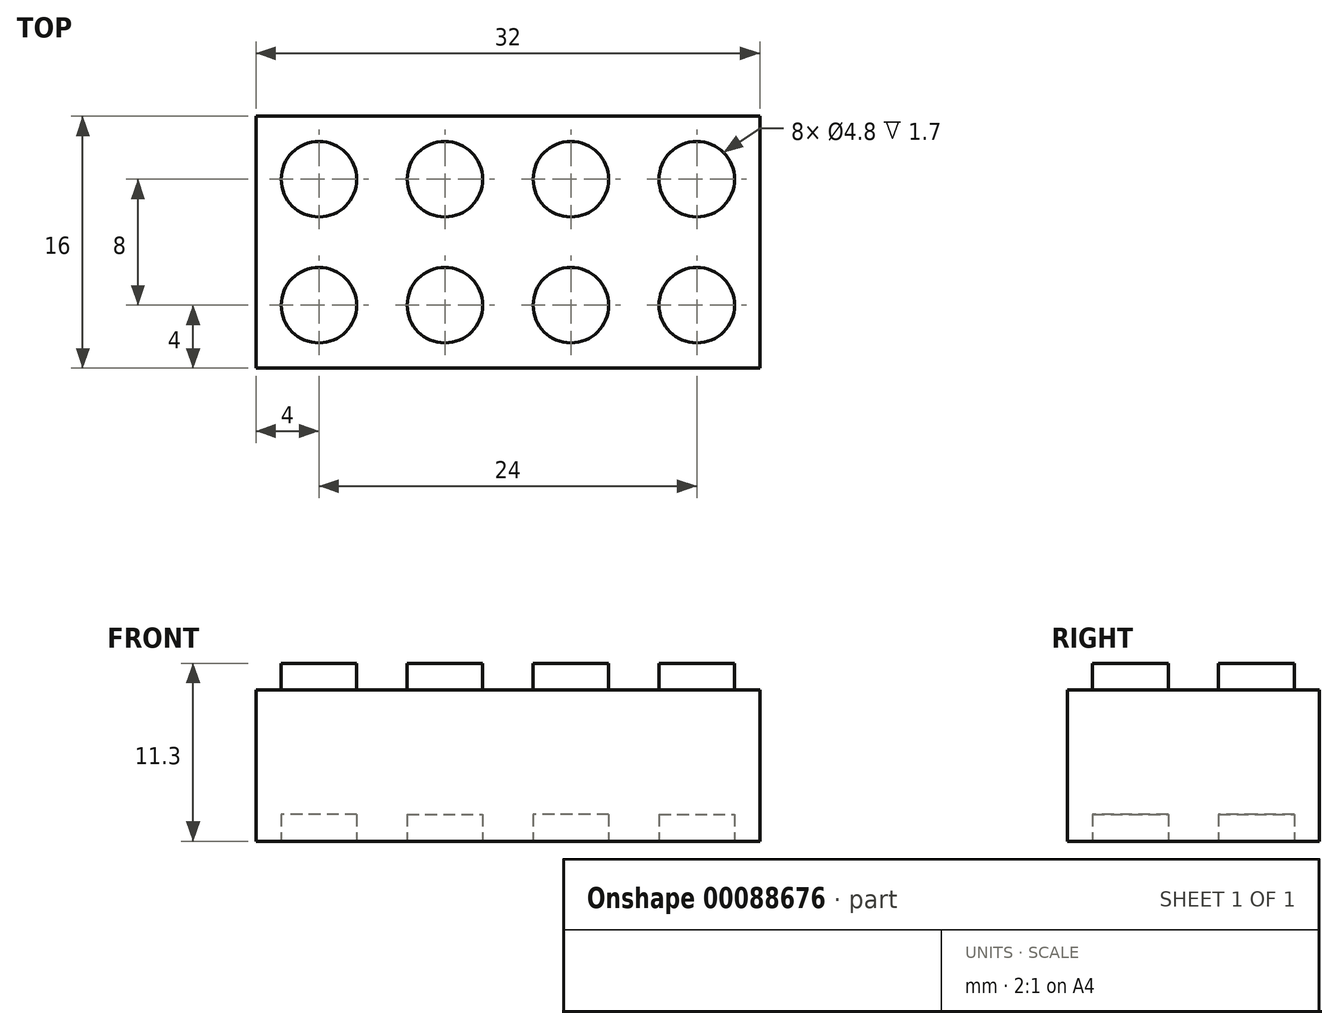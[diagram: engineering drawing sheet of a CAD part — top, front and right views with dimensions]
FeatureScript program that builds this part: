
annotation { "Feature Type Name" : "Feature", "Feature Type Description" : "" }
export const myFeature = defineFeature(function(context is Context, id is Id, definition is map)
    precondition{}
    {
        {
            var Q0;
            Q0=qCreatedBy(makeId("Front.planeOp"),FACE);
            var sketch = newSketch(context, id + "F0", { "sketchPlane" : qUnion([Q0])});
            skLineSegment(sketch, "E0.bottom", {"start": v(-4, 9.6) * mm, "end": v(-2.4, 9.6) * mm});
            skLineSegment(sketch, "E0.top", {"start": v(-4, 0) * mm, "end": v(4, 0) * mm});
            skLineSegment(sketch, "E0.left", {"start": v(-4, 9.6) * mm, "end": v(-4, 0) * mm});
            skLineSegment(sketch, "E0.right", {"start": v(4, 9.6) * mm, "end": v(4, 0) * mm});
            skLineSegment(sketch, "E1.top", {"start": v(-2.4, 11.3) * mm, "end": v(2.4, 11.3) * mm});
            skLineSegment(sketch, "E1.left", {"start": v(-2.4, 9.6) * mm, "end": v(-2.4, 11.3) * mm});
            skLineSegment(sketch, "E1.right", {"start": v(2.4, 9.6) * mm, "end": v(2.4, 11.3) * mm});
            skLineSegment(sketch, "E2", {"start": v(0, 0) * mm, "end": v(0, 24.04) * mm, "construction": true});
            skLineSegment(sketch, "E3.trimOffspring", {"start": v(2.4, 9.6) * mm, "end": v(4, 9.6) * mm});
            skSolve(sketch);
        }
        {
            var Q0;
            Q0=makeQuery(id+"F0.imprint","IMPRINT",FACE,{"disambiguationData":[TD([[makeQuery(id+"F0.imprint","IMPRINT",EDGE,{"derivedFrom":sQuery(id+"F0.wireOp",EDGE,"E0.bottom")}),-1.0]])]});
            extrude(context, id + "F1", {"entities" : qUnion([Q0]), "depth" : 8 * mm});
        }
        {
            var Q0;
            Q0=qCreatedBy(makeId("Top.planeOp"),FACE);
            var Q1;
            Q1=makeQuery(id+"F1.opExtrude","CAP_VERTEX",VERTEX,{"disambiguationData":[OSD([sQuery(id+"F0.wireOp",EDGE,"E1.top"),sQuery(id+"F0.wireOp",EDGE,"E1.right")])],"isStart":true});
            cPlane(context, id + "F2", {"entities" : qUnion([Q0, Q1]), "cplaneType" : CPlaneType.PLANE_POINT, "offset" : 152.4 * mm, "width" : 152.4 * mm, "height" : 152.4 * mm});
        }
        {
            var Q0;
            Q0=qCreatedBy(id+"F2.planeOp",FACE);
            var sketch = newSketch(context, id + "F3", { "sketchPlane" : qUnion([Q0])});
            skLineSegment(sketch, "E4.0", {"start": v(-4, -8) * mm, "end": v(-4, 0) * mm});
            skLineSegment(sketch, "E5.0", {"start": v(4, -8) * mm, "end": v(4, 0) * mm});
            skLineSegment(sketch, "E6", {"start": v(-4, 0) * mm, "end": v(4, 0) * mm});
            skLineSegment(sketch, "E7", {"start": v(-4, -8) * mm, "end": v(4, -8) * mm});
            skLineSegment(sketch, "E8", {"start": v(-4, 0) * mm, "end": v(4, -8) * mm, "construction": true});
            skLineSegment(sketch, "E9", {"start": v(-4, -8) * mm, "end": v(4, 0) * mm, "construction": true});
            skCircle(sketch, "E10", {"center": v(0, -4) * mm, "radius": 2.4 * mm});
            skSolve(sketch);
        }
        {
            var Q0;
            Q0=qSketchRegion(id+"F3",true);
            var Q1;
            Q1=makeQuery(id+"F1.opExtrude","SWEPT_FACE",FACE,{"disambiguationData":[OSD([sQuery(id+"F0.wireOp",EDGE,"E0.bottom")])]});
            extrude(context, id + "F4", {"entities" : qUnion([Q0]), "operationType" : NewBodyOperationType.REMOVE, "endBound" : BoundingType.UP_TO_SURFACE, "oppositeDirection" : true, "endBoundEntityFace" : qUnion([Q1]), "depth" : 25.4 * mm});
        }
        {
            var Q0;
            Q0=qCreatedBy(makeId("Top.planeOp"),FACE);
            var sketch = newSketch(context, id + "F5", { "sketchPlane" : qUnion([Q0])});
            skCircle(sketch, "E11.0", {"center": v(0, -4) * mm, "radius": 2.4 * mm});
            skSolve(sketch);
        }
        {
            var Q0;
            Q0=makeQuery(id+"F5.imprint","IMPRINT",FACE,{"disambiguationData":[TD([[makeQuery(id+"F5.imprint","IMPRINT",EDGE,{"derivedFrom":sQuery(id+"F5.wireOp",EDGE,"E11.0")}),1.0]])]});
            extrude(context, id + "F6", {"entities" : qUnion([Q0]), "operationType" : NewBodyOperationType.REMOVE, "depth" : 1.7 * mm});
        }
        {
            var Q0;
            Q0=qCreatedBy(makeId("Right.planeOp"),FACE);
            var Q1;
            Q1=makeQuery(id+"F1.opExtrude","CAP_VERTEX",VERTEX,{"disambiguationData":[OSD([sQuery(id+"F0.wireOp",EDGE,"E0.right"),sQuery(id+"F0.wireOp",EDGE,"E3.trimOffspring")])],"isStart":false});
            cPlane(context, id + "F7", {"entities" : qUnion([Q0, Q1]), "cplaneType" : CPlaneType.PLANE_POINT, "offset" : 152.4 * mm, "width" : 152.4 * mm, "height" : 152.4 * mm});
        }
        {
            var Q0;
            Q0=makeQuery(id+"F1.opExtrude","SWEPT_BODY",BODY,{"disambiguationData":[OSD([sQuery(id+"F0.wireOp",EDGE,"E0.bottom"),sQuery(id+"F0.wireOp",EDGE,"E0.top"),sQuery(id+"F0.wireOp",EDGE,"E0.left"),sQuery(id+"F0.wireOp",EDGE,"E0.right"),sQuery(id+"F0.wireOp",EDGE,"E1.top"),sQuery(id+"F0.wireOp",EDGE,"E1.left"),sQuery(id+"F0.wireOp",EDGE,"E1.right"),sQuery(id+"F0.wireOp",EDGE,"E3.trimOffspring")])]});
            var Q1;
            Q1=qCreatedBy(id+"F7.planeOp",FACE);
            mirror(context, id + "F8", {"operationType" : NewBodyOperationType.ADD, "entities" : qUnion([Q0]), "mirrorPlane" : qUnion([Q1])});
        }
        {
            var Q0;
            Q0=makeQuery(id+"F1.opExtrude","SWEPT_BODY",BODY,{"disambiguationData":[OSD([sQuery(id+"F0.wireOp",EDGE,"E0.bottom"),sQuery(id+"F0.wireOp",EDGE,"E0.top"),sQuery(id+"F0.wireOp",EDGE,"E0.left"),sQuery(id+"F0.wireOp",EDGE,"E0.right"),sQuery(id+"F0.wireOp",EDGE,"E1.top"),sQuery(id+"F0.wireOp",EDGE,"E1.left"),sQuery(id+"F0.wireOp",EDGE,"E1.right"),sQuery(id+"F0.wireOp",EDGE,"E3.trimOffspring")])]});
            var Q1;
            Q1=qCreatedBy(makeId("Front.planeOp"),FACE);
            mirror(context, id + "F9", {"operationType" : NewBodyOperationType.ADD, "entities" : qUnion([Q0]), "mirrorPlane" : qUnion([Q1])});
        }
        {
            var Q0;
            Q0=qCreatedBy(id+"F7.planeOp",FACE);
            var Q1;
            Q1=makeQuery(id+"F9.opPattern","COPY",VERTEX,{"derivedFrom":makeQuery(id+"F8.opPattern","COPY",VERTEX,{"derivedFrom":makeQuery(id+"F1.opExtrude","CAP_VERTEX",VERTEX,{"disambiguationData":[OSD([sQuery(id+"F0.wireOp",EDGE,"E0.bottom"),sQuery(id+"F0.wireOp",EDGE,"E0.left")])],"isStart":false}),"instanceName":"1"}),"instanceName":"1"});
            cPlane(context, id + "F10", {"entities" : qUnion([Q0, Q1]), "cplaneType" : CPlaneType.PLANE_POINT, "offset" : 152.4 * mm, "width" : 152.4 * mm, "height" : 152.4 * mm});
        }
        {
            var Q0;
            Q0=makeQuery(id+"F1.opExtrude","SWEPT_BODY",BODY,{"disambiguationData":[OSD([sQuery(id+"F0.wireOp",EDGE,"E0.bottom"),sQuery(id+"F0.wireOp",EDGE,"E0.top"),sQuery(id+"F0.wireOp",EDGE,"E0.left"),sQuery(id+"F0.wireOp",EDGE,"E0.right"),sQuery(id+"F0.wireOp",EDGE,"E1.top"),sQuery(id+"F0.wireOp",EDGE,"E1.left"),sQuery(id+"F0.wireOp",EDGE,"E1.right"),sQuery(id+"F0.wireOp",EDGE,"E3.trimOffspring")])]});
            var Q1;
            Q1=qCreatedBy(id+"F10.planeOp",FACE);
            mirror(context, id + "F11", {"operationType" : NewBodyOperationType.ADD, "entities" : qUnion([Q0]), "mirrorPlane" : qUnion([Q1])});
        }
    });
